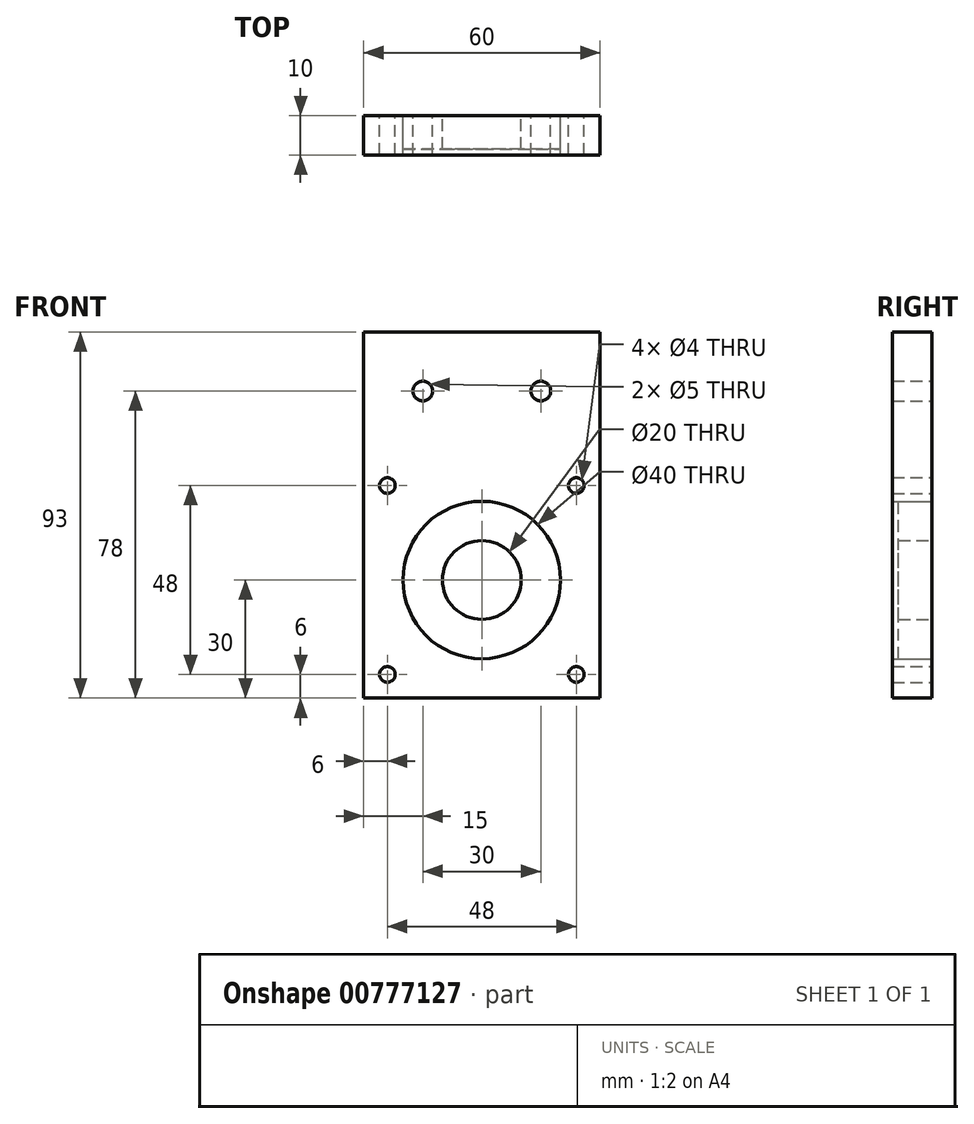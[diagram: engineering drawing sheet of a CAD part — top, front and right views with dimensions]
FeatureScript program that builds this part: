
annotation { "Feature Type Name" : "Feature", "Feature Type Description" : "" }
export const myFeature = defineFeature(function(context is Context, id is Id, definition is map)
    precondition{}
    {
        {
            var Q0;
            Q0=qCreatedBy(makeId("Front.planeOp"),FACE);
            var sketch = newSketch(context, id + "F0", { "sketchPlane" : qUnion([Q0])});
            skLineSegment(sketch, "E0.bottom", {"start": v(-54, 93) * mm, "end": v(6, 93) * mm});
            skLineSegment(sketch, "E0.top", {"start": v(-54, 0) * mm, "end": v(6, 0) * mm});
            skLineSegment(sketch, "E0.left", {"start": v(-54, 93) * mm, "end": v(-54, 0) * mm});
            skLineSegment(sketch, "E0.right", {"start": v(6, 93) * mm, "end": v(6, 0) * mm});
            skCircle(sketch, "E1", {"center": v(-39, 78) * mm, "radius": 2.5 * mm});
            skCircle(sketch, "E2", {"center": v(-9, 78) * mm, "radius": 2.5 * mm});
            skCircle(sketch, "E3", {"center": v(-24, 30) * mm, "radius": 10 * mm});
            skPoint(sketch, "E3.centerSnap0", {"position": v(-24, 0) * mm});
            skCircle(sketch, "E4", {"center": v(-48, 54) * mm, "radius": 2 * mm});
            skCircle(sketch, "E5", {"center": v(0, 54) * mm, "radius": 2 * mm});
            skCircle(sketch, "E6", {"center": v(0, 6) * mm, "radius": 2 * mm});
            skCircle(sketch, "E7", {"center": v(-48, 6) * mm, "radius": 2 * mm});
            skCircle(sketch, "E8", {"center": v(-24, 30) * mm, "radius": 20 * mm});
            skSolve(sketch);
        }
        {
            var Q0;
            Q0 = qSketchRegion(id + "F0", true);
            extrude(context, id + "F1", {"entities" : qUnion([Q0]), "depth" : 10 * mm, "offsetDistance" : 25 * mm});
        }
        {
            var Q0;
            Q0=makeQuery(id+"F0.imprint","IMPRINT",FACE,{"disambiguationData":[TD([[makeQuery(id+"F0.imprint","IMPRINT",EDGE,{"derivedFrom":sQuery(id+"F0.wireOp",EDGE,"E3")}),-1.0]])]});
            extrude(context, id + "F2", {"entities" : qUnion([Q0]), "depth" : 8.5 * mm, "offsetDistance" : 25 * mm});
        }
    });
